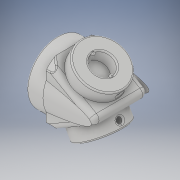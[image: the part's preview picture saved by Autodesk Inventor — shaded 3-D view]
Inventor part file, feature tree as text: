
AUTODESK INVENTOR PART (.ipt)
format: ipt  version: 2019 (Build 230136000, 136)  size: 518,144 bytes
history: native  units: in
note: dims shown in document units (in); Inventor stores cm internally (conversion verified against a paired STEP export)
features: sketch x17, extrude x9, fillet x6, plane x4, mirror x3, projected_geometry x3, thread x2, sweep x1
ambient origin geometry x8: Origin, YZ Plane, XZ Plane, XY Plane, X Axis, Y Axis, Z Axis, Center Point
bodies: Solid2 (feature_tree)
feature tree (45):
  extrude  "Extrusion6"  Depth=0.4724in TaperAngle=0.0deg
  extrude  "Extrusion7"  Depth=0.4724in TaperAngle=0.0deg
  sketch  "Sketch11"  dims[d34=0.0098in d35=45.0deg]
  extrude  "Extrusion9"  TaperAngle=45.0deg  [1 undecoded]
  sketch  "Sketch21"  dims[d70=1.9685in d71=0.0in d72=11.811in d73=0.0in d76=60.0deg]
  extrude  "Extrusion13"  TaperAngle=60.0deg  [1 undecoded]
  sketch  "Sketch26"  dims[d98=0.9449in d99=0.7874in d100=1.7323in d101=0.1417in d102=0.4724in d103=0.0in d104=0.2047in d105=0.315in d106=0.0in d107=0.3937in d108=0.0in d109=0.1969in]
  plane  "Work Plane5"
  extrude  "Extrusion15"  Depth=11.811in TaperAngle=0.0deg
  thread  "Thread3"  [1 undecoded]
  plane  "Work Plane7"
  mirror  "Mirror3"
  extrude  "Extrusion14"  Depth=0.4724in TaperAngle=0.0deg
  extrude  "Extrusion18"  Depth=0.3937in
  sketch  "Sketch36"  dims[d117=0.0472in]
  plane  "Work Plane10"
  extrude  "Extrusion19"  Depth=0.3937in
  thread  "Thread5"  [1 undecoded]
  plane  "Work Plane11"
  mirror  "Mirror6"
  mirror  "Mirror7"
  fillet  "Fillet3"  Radius=0.1417in
  fillet  "Fillet5"  Radius=0.4724in
  fillet  "Fillet8"  Radius=0.2047in
  fillet  "Fillet9"  Radius=0.315in
  fillet  "Fillet10"  Radius=0.3937in
  fillet  "Fillet11"  Radius=0.1969in
  extrude  "Extrusion20"  Depth=0.0472in
  sweep  "Sweep1"
  sketch  "3D Sketch2"
  sketch  "Sketch8"  dims[d28=0.0118in d29=0.4724in d30=0.0in]
  projected_geometry  "Projected Loop1"
  sketch  "Sketch9"  dims[d31=0.2362in d32=0.4724in d33=0.0in]
  sketch  "Sketch13"  dims[d42=0.1181in d43=0.0in d69=60.0deg]
  sketch  "Sketch22"  dims[d81=0.1969in d82=0.4724in d83=0.0in]
  sketch  "Sketch23"  dims[d84=0.3937in d85=0.0in d97=2.5591in]
  sketch  "Sketch28"  dims[d111=0.0787in d114=0.0472in]
  sketch  "Sketch34"  dims[d115=0.0472in d116=0.0472in]
  sketch  "Sketch37"  dims[d120=0.0in d121=0.0in]
  sketch  "3D Sketch3"
  sketch  "Sketch38"  dims[d122=0.1575in]
  sketch  "3D Sketch4"
  sketch  "Sketch39"  dims[d123=1.9685in d124=-0.0137in]
  projected_geometry  "Projected Loop4"
  projected_geometry  "Projected Loop5"
note: 4 required parameter values undecoded (feature->parameter linkage not recoverable at this tier; creation-order binding heuristic only, values carry confidence <= 0.55)
